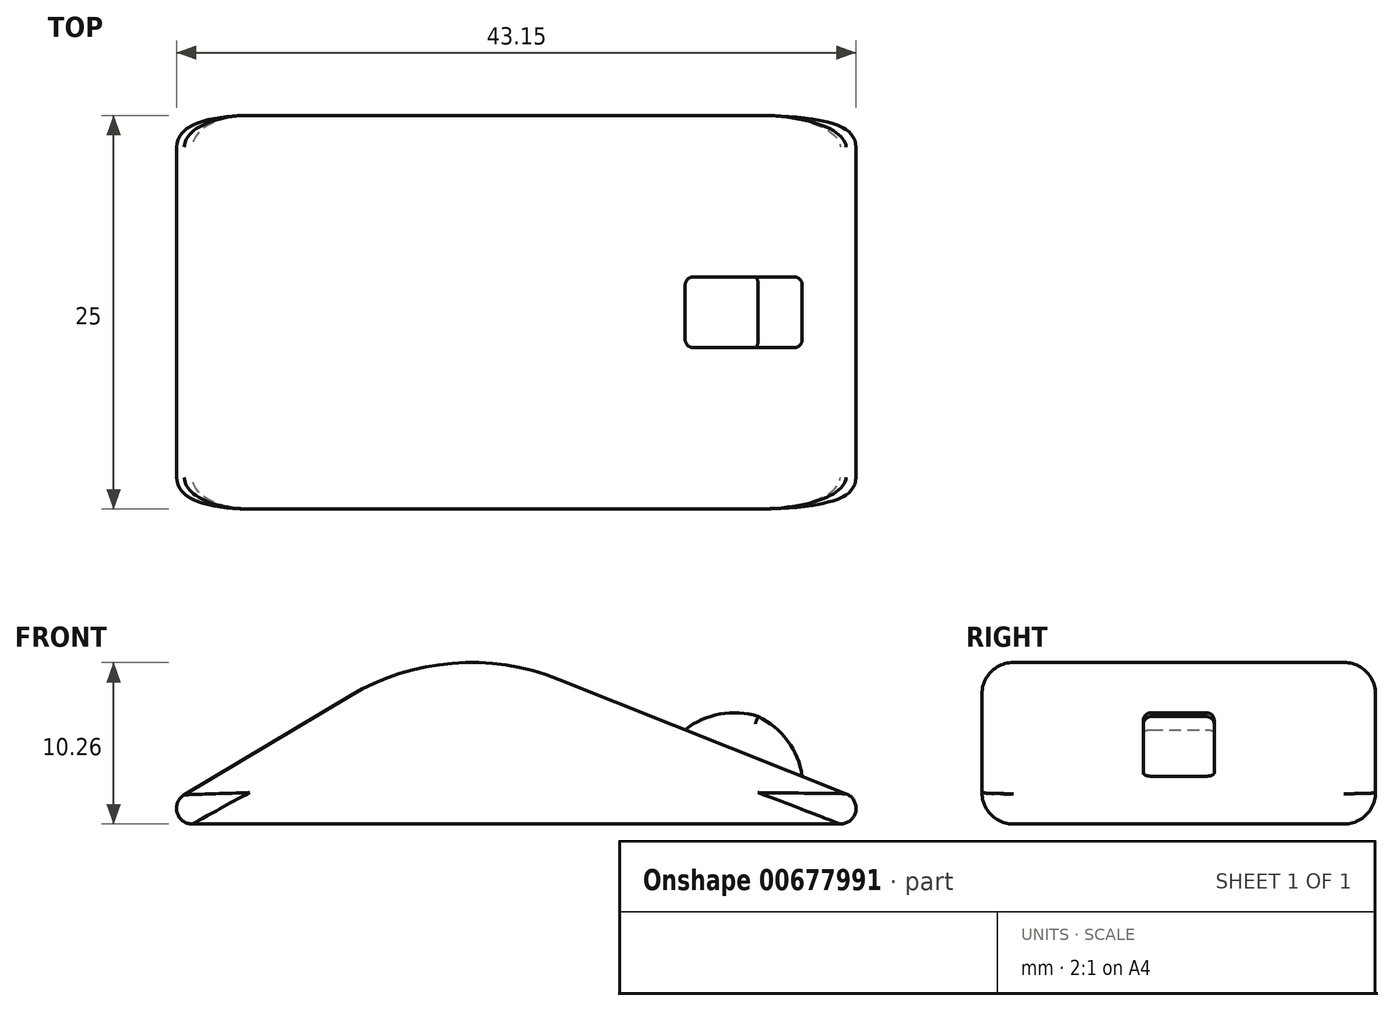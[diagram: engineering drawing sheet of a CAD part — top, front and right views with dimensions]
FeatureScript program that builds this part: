
annotation { "Feature Type Name" : "Feature", "Feature Type Description" : "" }
export const myFeature = defineFeature(function(context is Context, id is Id, definition is map)
    precondition{}
    {
        {
            var Q0;
            Q0=qCreatedBy(makeId("Front.planeOp"),FACE);
            var sketch = newSketch(context, id + "F0", { "sketchPlane" : qUnion([Q0])});
            skLineSegment(sketch, "E0", {"start": v(-20, 0) * mm, "end": v(30, 0) * mm});
            skLineSegment(sketch, "E1", {"start": v(30, 0) * mm, "end": v(0, 11.94) * mm});
            skLineSegment(sketch, "E2", {"start": v(0, 11.94) * mm, "end": v(-20, 0) * mm});
            skSolve(sketch);
        }
        {
            var Q0;
            Q0=makeQuery(id+"F0.imprint","IMPRINT",FACE,{"disambiguationData":[TD([[makeQuery(id+"F0.imprint","IMPRINT",EDGE,{"derivedFrom":sQuery(id+"F0.wireOp",EDGE,"E0")}),1.0]])]});
            extrude(context, id + "F1", {"entities" : qUnion([Q0]), "depth" : 25 * mm, "offsetDistance" : 25 * mm});
        }
        {
            var Q0;
            Q0=makeQuery(id+"F1.opExtrude","SWEPT_EDGE",EDGE,{"disambiguationData":[OSD([sQuery(id+"F0.wireOp",EDGE,"E1"),sQuery(id+"F0.wireOp",EDGE,"E2")])]});
            fillet(context, id + "F2", {"entities" : qUnion([Q0]), "radius" : 15 * mm, "tangentPropagation" : true, "allowEdgeOverflow" : false});
        }
        {
            var Q0;
            Q0=makeQuery(id+"F1.opExtrude","SWEPT_EDGE",EDGE,{"disambiguationData":[OSD([sQuery(id+"F0.wireOp",EDGE,"E0"),sQuery(id+"F0.wireOp",EDGE,"E1")])]});
            fillet(context, id + "F3", {"entities" : qUnion([Q0]), "radius" : 1 * mm, "tangentPropagation" : true, "allowEdgeOverflow" : false});
        }
        {
            var Q0;
            Q0=makeQuery(id+"F1.opExtrude","SWEPT_EDGE",EDGE,{"disambiguationData":[OSD([sQuery(id+"F0.wireOp",EDGE,"E0"),sQuery(id+"F0.wireOp",EDGE,"E2")])]});
            fillet(context, id + "F4", {"entities" : qUnion([Q0]), "radius" : 1 * mm, "tangentPropagation" : true, "allowEdgeOverflow" : false});
        }
        {
            var Q0;
            Q0=makeQuery(id+"F1.opExtrude","CAP_EDGE",EDGE,{"disambiguationData":[OSD([sQuery(id+"F0.wireOp",EDGE,"E1")])],"isStart":false});
            var Q1;
            Q1=makeQuery(id+"F1.opExtrude","CAP_EDGE",EDGE,{"disambiguationData":[OSD([sQuery(id+"F0.wireOp",EDGE,"E2")])],"isStart":false});
            var Q2;
            Q2=makeQuery(id+"F1.opExtrude","CAP_EDGE",EDGE,{"disambiguationData":[OSD([sQuery(id+"F0.wireOp",EDGE,"E1")])],"isStart":true});
            var Q3;
            Q3=makeQuery(id+"F1.opExtrude","CAP_EDGE",EDGE,{"disambiguationData":[OSD([sQuery(id+"F0.wireOp",EDGE,"E2")])],"isStart":true});
            fillet(context, id + "F5", {"entities" : qUnion([Q0, Q1, Q2, Q3]), "radius" : 2 * mm, "tangentPropagation" : true, "allowEdgeOverflow" : false});
        }
        {
            var Q0;
            Q0=makeQuery(id+"F1.opExtrude","SWEPT_FACE",FACE,{"disambiguationData":[OSD([sQuery(id+"F0.wireOp",EDGE,"E1")])]});
            var sketch = newSketch(context, id + "F6", { "sketchPlane" : qUnion([Q0])});
            skLineSegment(sketch, "E3.bottom", {"start": v(11.66, -14.75) * mm, "end": v(19.66, -14.75) * mm});
            skLineSegment(sketch, "E3.top", {"start": v(11.66, -10.25) * mm, "end": v(19.66, -10.25) * mm});
            skLineSegment(sketch, "E3.left", {"start": v(11.66, -14.75) * mm, "end": v(11.66, -10.25) * mm});
            skLineSegment(sketch, "E3.right", {"start": v(19.66, -14.75) * mm, "end": v(19.66, -10.25) * mm});
            skPoint(sketch, "E4", {"position": v(22.66, -12.5) * mm});
            skPoint(sketch, "E5", {"position": v(2.99, -12.5) * mm});
            skLineSegment(sketch, "E6", {"start": v(2.99, -12.5) * mm, "end": v(22.66, -12.5) * mm, "construction": true});
            skSolve(sketch);
        }
        {
            var Q0;
            Q0=makeQuery(id+"F6.imprint","IMPRINT",FACE,{"disambiguationData":[TD([[makeQuery(id+"F6.imprint","IMPRINT",EDGE,{"derivedFrom":sQuery(id+"F6.wireOp",EDGE,"E3.bottom")}),1.0]])]});
            extrude(context, id + "F7", {"entities" : qUnion([Q0]), "operationType" : NewBodyOperationType.ADD, "endBound" : BoundingType.SYMMETRIC, "depth" : 5 * mm, "offsetDistance" : 25 * mm});
        }
        {
            var Q0;
            Q0=makeQuery(id+"F7.opExtrude","CAP_EDGE",EDGE,{"disambiguationData":[OSD([sQuery(id+"F6.wireOp",EDGE,"E3.left")])],"isStart":false});
            var Q1;
            Q1=makeQuery(id+"F7.opExtrude","CAP_EDGE",EDGE,{"disambiguationData":[OSD([sQuery(id+"F6.wireOp",EDGE,"E3.right")])],"isStart":false});
            fillet(context, id + "F8", {"entities" : qUnion([Q0, Q1]), "radius" : 5 * mm, "tangentPropagation" : true, "allowEdgeOverflow" : false});
        }
        {
            var Q0;
            Q0=makeQuery(id+"F8.opFillet","BLEND_EDGE",EDGE,{"blendedFrom":[makeQuery(id+"F7.opExtrude","CAP_EDGE",EDGE,{"disambiguationData":[OSD([sQuery(id+"F6.wireOp",EDGE,"E3.right")])],"isStart":false}),makeQuery(id+"F7.opExtrude","SWEPT_FACE",FACE,{"disambiguationData":[OSD([sQuery(id+"F6.wireOp",EDGE,"E3.bottom")])]})],"blendedInto":[makeQuery(id+"F7.opExtrude","SWEPT_FACE",FACE,{"disambiguationData":[OSD([sQuery(id+"F6.wireOp",EDGE,"E3.bottom")])]})]});
            var Q1;
            Q1=makeQuery(id+"F8.opFillet","BLEND_EDGE",EDGE,{"blendedFrom":[makeQuery(id+"F7.opExtrude","CAP_EDGE",EDGE,{"disambiguationData":[OSD([sQuery(id+"F6.wireOp",EDGE,"E3.left")])],"isStart":false}),makeQuery(id+"F7.opExtrude","SWEPT_FACE",FACE,{"disambiguationData":[OSD([sQuery(id+"F6.wireOp",EDGE,"E3.top")])]})],"blendedInto":[makeQuery(id+"F7.opExtrude","SWEPT_FACE",FACE,{"disambiguationData":[OSD([sQuery(id+"F6.wireOp",EDGE,"E3.top")])]})]});
            var Q2;
            Q2=makeQuery(id+"F8.opFillet","BLEND_EDGE",EDGE,{"blendedFrom":[makeQuery(id+"F7.opExtrude","CAP_EDGE",EDGE,{"disambiguationData":[OSD([sQuery(id+"F6.wireOp",EDGE,"E3.right")])],"isStart":false}),makeQuery(id+"F7.opExtrude","SWEPT_FACE",FACE,{"disambiguationData":[OSD([sQuery(id+"F6.wireOp",EDGE,"E3.top")])]})],"blendedInto":[makeQuery(id+"F7.opExtrude","SWEPT_FACE",FACE,{"disambiguationData":[OSD([sQuery(id+"F6.wireOp",EDGE,"E3.top")])]})]});
            var Q3;
            Q3=makeQuery(id+"F8.opFillet","BLEND_EDGE",EDGE,{"blendedFrom":[makeQuery(id+"F7.opExtrude","CAP_EDGE",EDGE,{"disambiguationData":[OSD([sQuery(id+"F6.wireOp",EDGE,"E3.left")])],"isStart":false}),makeQuery(id+"F7.opExtrude","SWEPT_FACE",FACE,{"disambiguationData":[OSD([sQuery(id+"F6.wireOp",EDGE,"E3.bottom")])]})],"blendedInto":[makeQuery(id+"F7.opExtrude","SWEPT_FACE",FACE,{"disambiguationData":[OSD([sQuery(id+"F6.wireOp",EDGE,"E3.bottom")])]})]});
            fillet(context, id + "F9", {"entities" : qUnion([Q0, Q1, Q2, Q3]), "radius" : 0.5 * mm, "tangentPropagation" : true, "allowEdgeOverflow" : false});
        }
    });
